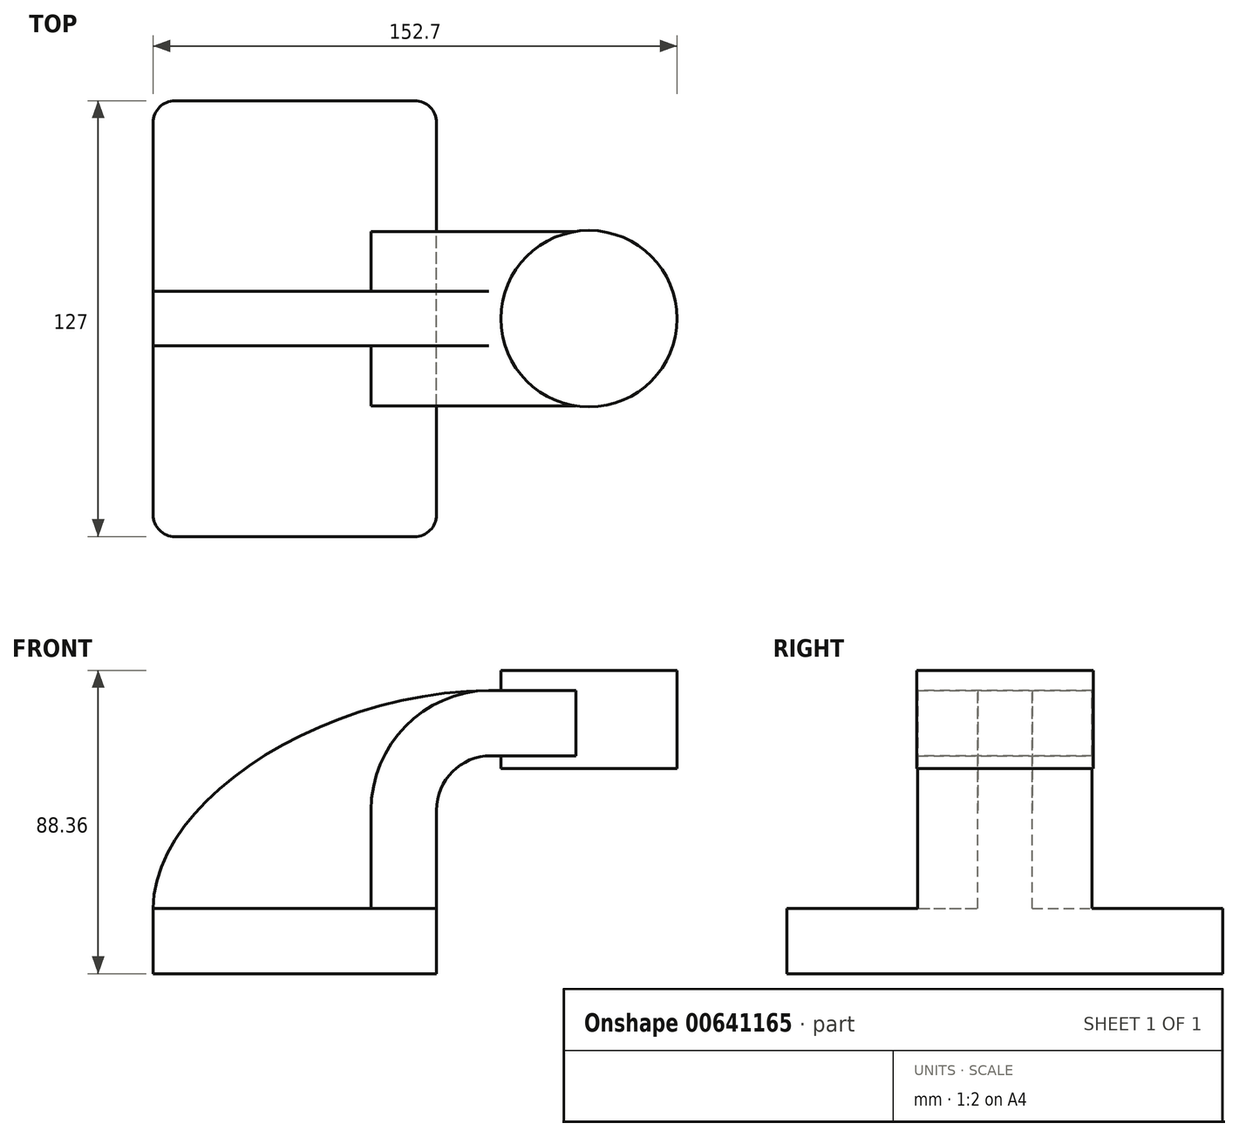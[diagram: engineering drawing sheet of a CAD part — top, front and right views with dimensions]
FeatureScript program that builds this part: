
annotation { "Feature Type Name" : "Feature", "Feature Type Description" : "" }
export const myFeature = defineFeature(function(context is Context, id is Id, definition is map)
    precondition{}
    {
        {
            var Q0;
            Q0=qCreatedBy(makeId("Front.planeOp"),FACE);
            var sketch = newSketch(context, id + "F0", { "sketchPlane" : qUnion([Q0])});
            skLineSegment(sketch, "E0.bottom", {"start": v(41.28, -9.52) * mm, "end": v(-41.27, -9.52) * mm});
            skLineSegment(sketch, "E0.top", {"start": v(41.27, 9.53) * mm, "end": v(-41.27, 9.53) * mm});
            skLineSegment(sketch, "E0.left", {"start": v(41.28, -9.52) * mm, "end": v(41.27, 9.53) * mm});
            skLineSegment(sketch, "E0.right", {"start": v(-41.27, -9.52) * mm, "end": v(-41.28, 9.53) * mm});
            skPoint(sketch, "E0.middle", {"position": v(0, 0) * mm});
            skLineSegment(sketch, "E1", {"start": v(41.27, 9.53) * mm, "end": v(41.27, 38.1) * mm});
            skArc(sketch, "E2", {"start": v(41.27, 38.1) * mm, "mid": v(45.92, 49.33) * mm, "end": v(57.15, 53.98) * mm});
            skLineSegment(sketch, "E3", {"start": v(57.15, 53.98) * mm, "end": v(85.73, 53.98) * mm});
            skLineSegment(sketch, "E4.0", {"start": v(57.15, 73.03) * mm, "end": v(85.73, 73.03) * mm});
            skArc(sketch, "E4.1", {"start": v(22.23, 38.1) * mm, "mid": v(32.45, 62.8) * mm, "end": v(57.15, 73.03) * mm});
            skLineSegment(sketch, "E4.2", {"start": v(22.22, 9.53) * mm, "end": v(22.22, 38.1) * mm});
            skFitSpline(sketch, "E5", {"points": [v(-41.28, 9.53) * mm, v(57.15, 73.03) * mm], "startDerivative": vector(0.1, 92.78) * mm, "endDerivative": vector(150.03, 0.95) * mm});
            skLineSegment(sketch, "E6.bottom", {"start": v(60.62, 78.83) * mm, "end": v(111.42, 78.83) * mm});
            skLineSegment(sketch, "E6.top", {"start": v(60.62, 50.25) * mm, "end": v(111.42, 50.25) * mm});
            skLineSegment(sketch, "E6.left", {"start": v(60.62, 78.83) * mm, "end": v(60.62, 50.25) * mm});
            skLineSegment(sketch, "E6.right", {"start": v(111.42, 78.83) * mm, "end": v(111.42, 50.25) * mm});
            skLineSegment(sketch, "E7", {"start": v(85.73, 78.83) * mm, "end": v(85.73, 50.25) * mm});
            skPoint(sketch, "E7.startSnap0", {"position": v(86.02, 78.83) * mm});
            skSolve(sketch);
        }
        {
            var Q0;
            Q0=makeQuery(id+"F0.imprint","IMPRINT",FACE,{"disambiguationData":[TD([[makeQuery(id+"F0.imprint","IMPRINT",EDGE,{"derivedFrom":sQuery(id+"F0.wireOp",EDGE,"E0.bottom")}),-1.0]])]});
            extrude(context, id + "F1", {"entities" : qUnion([Q0]), "endBound" : BoundingType.SYMMETRIC, "depth" : 127 * mm, "offsetDistance" : 25.4 * mm});
        }
        {
            var Q0;
            {var subQ4=sQuery(id+"F0.wireOp",EDGE,"E1");Q0=makeQuery(id+"F0.imprint","IMPRINT",FACE,{"disambiguationData":[TD([[makeQuery(id+"F0.imprint","IMPRINT",EDGE,{"derivedFrom":subQ4}),1.0]])]});}
            extrude(context, id + "F2", {"entities" : qUnion([Q0]), "operationType" : NewBodyOperationType.ADD, "endBound" : BoundingType.SYMMETRIC, "depth" : 50.8 * mm, "offsetDistance" : 25.4 * mm});
        }
        {
            var Q0;
            {var subQ3=sQuery(id+"F0.wireOp",EDGE,"E4.2");Q0=makeQuery(id+"F0.imprint","IMPRINT",FACE,{"disambiguationData":[TD([[makeQuery(id+"F0.imprint","IMPRINT",EDGE,{"derivedFrom":subQ3}),1.0]])]});}
            extrude(context, id + "F3", {"entities" : qUnion([Q0]), "operationType" : NewBodyOperationType.ADD, "endBound" : BoundingType.SYMMETRIC, "depth" : 15.88 * mm, "offsetDistance" : 25.4 * mm});
        }
        {
            var Q0;
            {var subQ0=sQuery(id+"F0.wireOp",EDGE,"E7");var subQ1=sQuery(id+"F0.wireOp",EDGE,"E3");var subQ2=makeQuery(id+"F0.imprint","INTERSECT",VERTEX,{"derivedFrom":[subQ1,subQ0]});Q0=makeQuery(id+"F0.imprint","IMPRINT",FACE,{"disambiguationData":[TD([[makeQuery(id+"F0.imprint","IMPRINT",EDGE,{"disambiguationData":[TD([[subQ2,1.0]])],"derivedFrom":subQ1}),1.0]])]});}
            extrude(context, id + "F4", {"entities" : qUnion([Q0]), "operationType" : NewBodyOperationType.ADD, "endBound" : BoundingType.SYMMETRIC, "depth" : 50.8 * mm, "offsetDistance" : 25.4 * mm});
        }
        {
            var Q0;
            {var subQ0=sQuery(id+"F0.wireOp",EDGE,"E6.right");Q0=makeQuery(id+"F0.imprint","IMPRINT",FACE,{"disambiguationData":[TD([[makeQuery(id+"F0.imprint","IMPRINT",EDGE,{"derivedFrom":subQ0}),-1.0]])]});}
            var Q1;
            Q1=sQuery(id+"F0.wireOp",EDGE,"E7");
            revolve(context, id + "F5", {"operationType" : NewBodyOperationType.ADD, "entities" : qUnion([Q0]), "axis" : qUnion([Q1]), "revolveType" : RevolveType.FULL});
        }
        {
            var Q0;
            Q0=makeQuery(id+"F1.opExtrude","CAP_EDGE",EDGE,{"disambiguationData":[OSD([sQuery(id+"F0.wireOp",EDGE,"E0.right")])],"isStart":false});
            var Q1;
            Q1=makeQuery(id+"F1.opExtrude","CAP_EDGE",EDGE,{"disambiguationData":[OSD([sQuery(id+"F0.wireOp",EDGE,"E0.left")])],"isStart":false});
            var Q2;
            Q2=makeQuery(id+"F1.opExtrude","CAP_EDGE",EDGE,{"disambiguationData":[OSD([sQuery(id+"F0.wireOp",EDGE,"E0.left")])],"isStart":true});
            var Q3;
            Q3=makeQuery(id+"F1.opExtrude","CAP_EDGE",EDGE,{"disambiguationData":[OSD([sQuery(id+"F0.wireOp",EDGE,"E0.right")])],"isStart":true});
            fillet(context, id + "F6", {"entities" : qUnion([Q0, Q1, Q2, Q3]), "radius" : 6.35 * mm, "tangentPropagation" : true, "allowEdgeOverflow" : false});
        }
    });
